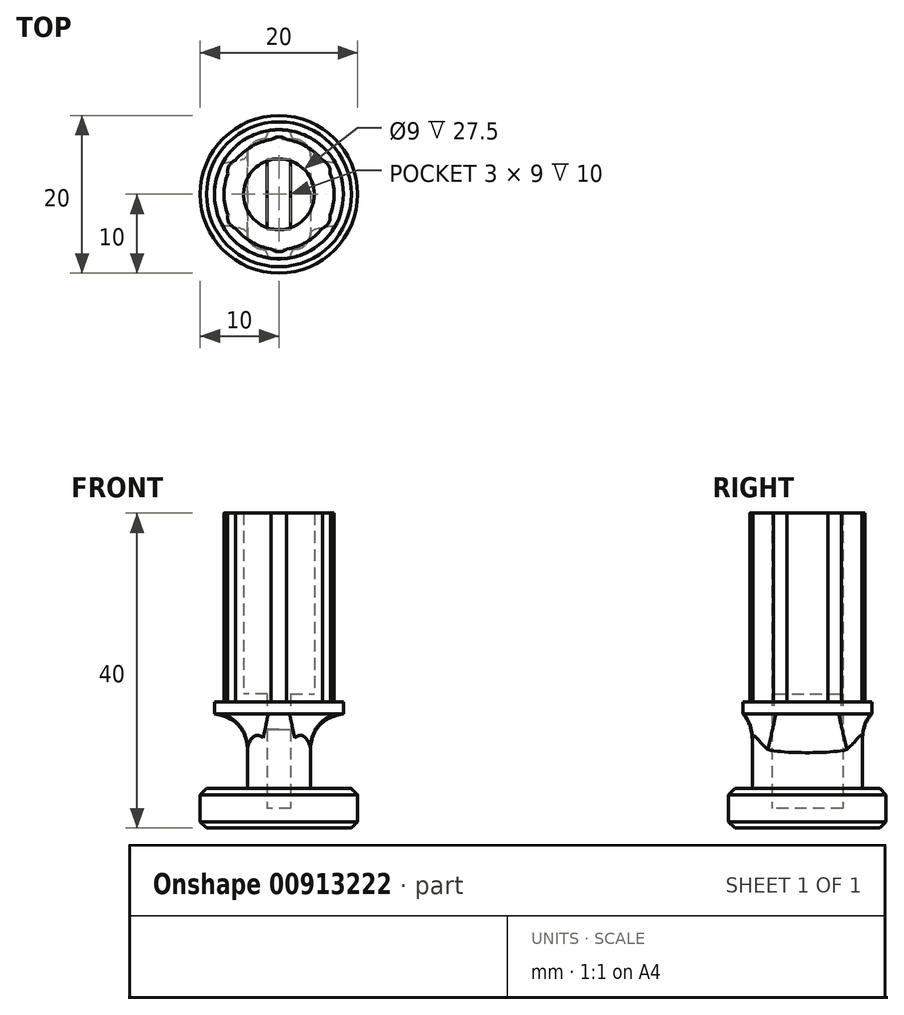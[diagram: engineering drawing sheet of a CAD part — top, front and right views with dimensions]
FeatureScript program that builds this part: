
annotation { "Feature Type Name" : "Feature", "Feature Type Description" : "" }
export const myFeature = defineFeature(function(context is Context, id is Id, definition is map)
    precondition{}
    {
        {
            var Q0;
            Q0=qCreatedBy(makeId("Top.planeOp"),FACE);
            var sketch = newSketch(context, id + "F0", { "sketchPlane" : qUnion([Q0])});
            skCircle(sketch, "E0", {"center": v(0, 0) * mm, "radius": 10 * mm});
            skArc(sketch, "E1", {"start": v(-0.99, 6.93) * mm, "mid": v(-3.5, 6.06) * mm, "end": v(-5.5, 4.32) * mm});
            skArc(sketch, "E2", {"start": v(0.99, 6.93) * mm, "mid": v(0, 7.3) * mm, "end": v(-0.99, 6.93) * mm});
            skArc(sketch, "E3.1.0", {"start": v(-5.5, 4.32) * mm, "mid": v(-6.32, 3.65) * mm, "end": v(-6.5, 2.61) * mm});
            skArc(sketch, "E3.2.0", {"start": v(-6.5, -2.61) * mm, "mid": v(-6.32, -3.65) * mm, "end": v(-5.5, -4.32) * mm});
            skArc(sketch, "E3.3.0", {"start": v(-0.99, -6.93) * mm, "mid": v(0, -7.3) * mm, "end": v(0.99, -6.93) * mm});
            skArc(sketch, "E3.4.0", {"start": v(5.5, -4.32) * mm, "mid": v(6.32, -3.65) * mm, "end": v(6.5, -2.61) * mm});
            skArc(sketch, "E3.5.0", {"start": v(6.5, 2.61) * mm, "mid": v(6.32, 3.65) * mm, "end": v(5.5, 4.32) * mm});
            skArc(sketch, "E4.trimOffspring", {"start": v(5.5, 4.32) * mm, "mid": v(3.5, 6.06) * mm, "end": v(0.99, 6.93) * mm});
            skArc(sketch, "E5.trimOffspring", {"start": v(-6.5, 2.61) * mm, "mid": v(-7, 0) * mm, "end": v(-6.5, -2.61) * mm});
            skArc(sketch, "E6.trimOffspring", {"start": v(-5.5, -4.32) * mm, "mid": v(-3.5, -6.06) * mm, "end": v(-0.99, -6.93) * mm});
            skArc(sketch, "E7.trimOffspring", {"start": v(0.99, -6.93) * mm, "mid": v(3.5, -6.06) * mm, "end": v(5.5, -4.32) * mm});
            skArc(sketch, "E8.trimOffspring", {"start": v(6.5, -2.61) * mm, "mid": v(7, 0) * mm, "end": v(6.5, 2.61) * mm});
            skPoint(sketch, "E9.middle", {"position": v(-0.44, -0.52) * mm});
            skCircle(sketch, "E10.0", {"center": v(0, 0) * mm, "radius": 8.2 * mm});
            skSolve(sketch);
        }
        {
            var Q0;
            Q0=makeQuery(id+"F0.imprint","IMPRINT",FACE,{"disambiguationData":[TD([[makeQuery(id+"F0.imprint","IMPRINT",EDGE,{"derivedFrom":sQuery(id+"F0.wireOp",EDGE,"E0")}),1.0]])]});
            var Q1;
            Q1=makeQuery(id+"F0.imprint","IMPRINT",FACE,{"disambiguationData":[TD([[makeQuery(id+"F0.imprint","IMPRINT",EDGE,{"derivedFrom":sQuery(id+"F0.wireOp",EDGE,"E1")}),-1.0]])]});
            extrude(context, id + "F1", {"entities" : qUnion([Q0, Q1]), "depth" : 5 * mm, "offsetDistance" : 25 * mm});
        }
        {
            var Q0;
            Q0=makeQuery(id+"F1.opExtrude","CAP_EDGE",EDGE,{"disambiguationData":[OSD([sQuery(id+"F0.wireOp",EDGE,"E0")])],"isStart":true});
            var Q1;
            Q1=makeQuery(id+"F1.opExtrude","CAP_EDGE",EDGE,{"disambiguationData":[OSD([sQuery(id+"F0.wireOp",EDGE,"E0")])],"isStart":false});
            chamfer(context, id + "F2", {"entities" : qUnion([Q0, Q1]), "width" : .8 * mm, "tangentPropagation" : true});
        }
        {
            var Q0;
            Q0=qCreatedBy(makeId("Top.planeOp"),FACE);
            var sketch = newSketch(context, id + "F3", { "sketchPlane" : qUnion([Q0])});
            skLineSegment(sketch, "E11.bottom", {"start": v(-4, -7) * mm, "end": v(4, -7) * mm});
            skLineSegment(sketch, "E11.top", {"start": v(-4, 7) * mm, "end": v(4, 7) * mm});
            skLineSegment(sketch, "E11.left", {"start": v(-4, -7) * mm, "end": v(-4, 7) * mm});
            skLineSegment(sketch, "E11.right", {"start": v(4, -7) * mm, "end": v(4, 7) * mm});
            skPoint(sketch, "E11.middle", {"position": v(0, 0) * mm});
            skSolve(sketch);
        }
        {
            var Q0;
            Q0 = qSketchRegion(id + "F3", true);
            extrude(context, id + "F4", {"entities" : qUnion([Q0]), "operationType" : NewBodyOperationType.ADD, "depth" : 15 * mm, "offsetDistance" : 25 * mm, "hasSecondDirection" : true, "secondDirectionOppositeDirection" : false, "secondDirectionDepth" : 2 * mm});
        }
        {
            var Q0;
            {var subQ1=sQuery(id+"F0.wireOp",EDGE,"E3.4.0");Q0=makeQuery(id+"F0.imprint","IMPRINT",FACE,{"disambiguationData":[TD([[makeQuery(id+"F0.imprint","IMPRINT",EDGE,{"derivedFrom":subQ1}),1.0]])]});}
            var Q1;
            {var subQ1=sQuery(id+"F0.wireOp",EDGE,"E3.1.0");Q1=makeQuery(id+"F0.imprint","IMPRINT",FACE,{"disambiguationData":[TD([[makeQuery(id+"F0.imprint","IMPRINT",EDGE,{"derivedFrom":subQ1}),1.0]])]});}
            var Q2;
            Q2=makeQuery(id+"F3.imprint","IMPRINT",FACE,{"disambiguationData":[TD([[makeQuery(id+"F3.imprint","IMPRINT",EDGE,{"derivedFrom":sQuery(id+"F3.wireOp",EDGE,"E11.bottom")}),1.0]])]});
            extrude(context, id + "F5", {"entities" : qUnion([Q0, Q1, Q2]), "operationType" : NewBodyOperationType.ADD, "depth" : 5 * mm, "offsetDistance" : 25 * mm});
        }
        {
            var Q0;
            {var subQ1=sQuery(id+"F0.wireOp",EDGE,"E3.4.0");Q0=makeQuery(id+"F0.imprint","IMPRINT",FACE,{"disambiguationData":[TD([[makeQuery(id+"F0.imprint","IMPRINT",EDGE,{"derivedFrom":subQ1}),1.0]])]});}
            var Q1;
            {var subQ1=sQuery(id+"F0.wireOp",EDGE,"E3.1.0");Q1=makeQuery(id+"F0.imprint","IMPRINT",FACE,{"disambiguationData":[TD([[makeQuery(id+"F0.imprint","IMPRINT",EDGE,{"derivedFrom":subQ1}),1.0]])]});}
            var Q2;
            {var subQ1=sQuery(id+"F0.wireOp",EDGE,"E2");Q2=makeQuery(id+"F0.imprint","IMPRINT",FACE,{"disambiguationData":[TD([[makeQuery(id+"F0.imprint","IMPRINT",EDGE,{"derivedFrom":subQ1}),1.0]])]});}
            extrude(context, id + "F6", {"entities" : qUnion([Q0, Q1, Q2]), "operationType" : NewBodyOperationType.ADD, "depth" : 40 * mm, "offsetDistance" : 25 * mm, "hasSecondDirection" : true, "secondDirectionOppositeDirection" : false, "secondDirectionDepth" : 14.5 * mm});
        }
        {
            var Q0;
            Q0=makeQuery(id+"F6.opExtrude","CAP_FACE",FACE,{"disambiguationData":[OSD([sQuery(id+"F0.wireOp",EDGE,"E1"),sQuery(id+"F0.wireOp",EDGE,"E2"),sQuery(id+"F0.wireOp",EDGE,"E3.1.0"),sQuery(id+"F0.wireOp",EDGE,"E3.2.0"),sQuery(id+"F0.wireOp",EDGE,"E3.3.0"),sQuery(id+"F0.wireOp",EDGE,"E3.4.0"),sQuery(id+"F0.wireOp",EDGE,"E3.5.0"),sQuery(id+"F0.wireOp",EDGE,"E4.trimOffspring"),sQuery(id+"F0.wireOp",EDGE,"E5.trimOffspring"),sQuery(id+"F0.wireOp",EDGE,"E6.trimOffspring"),sQuery(id+"F0.wireOp",EDGE,"E7.trimOffspring"),sQuery(id+"F0.wireOp",EDGE,"E8.trimOffspring")])],"isStart":false});
            shell(context, id + "F7", {"entities" : qUnion([Q0]), "thickness" : 2.5 * mm});
        }
        {
            var Q0;
            Q0=makeQuery(id+"F0.imprint","IMPRINT",FACE,{"disambiguationData":[TD([[makeQuery(id+"F0.imprint","IMPRINT",EDGE,{"derivedFrom":sQuery(id+"F0.wireOp",EDGE,"E1")}),-1.0]])]});
            extrude(context, id + "F8", {"entities" : qUnion([Q0]), "operationType" : NewBodyOperationType.ADD, "depth" : 16 * mm, "offsetDistance" : 25 * mm, "hasSecondDirection" : true, "secondDirectionOppositeDirection" : false, "secondDirectionDepth" : 14.5 * mm});
        }
        {
            var Q0;
            Q0=makeQuery(id+"F4.opExtrude","SWEPT_EDGE",EDGE,{"disambiguationData":[OSD([sQuery(id+"F3.wireOp",EDGE,"E11.bottom"),sQuery(id+"F3.wireOp",EDGE,"E11.right")])]});
            var Q1;
            Q1=makeQuery(id+"F4.opExtrude","SWEPT_EDGE",EDGE,{"disambiguationData":[OSD([sQuery(id+"F3.wireOp",EDGE,"E11.bottom"),sQuery(id+"F3.wireOp",EDGE,"E11.left")])]});
            var Q2;
            Q2=makeQuery(id+"F4.opExtrude","SWEPT_EDGE",EDGE,{"disambiguationData":[OSD([sQuery(id+"F3.wireOp",EDGE,"E11.top"),sQuery(id+"F3.wireOp",EDGE,"E11.right")])]});
            var Q3;
            Q3=makeQuery(id+"F4.opExtrude","SWEPT_EDGE",EDGE,{"disambiguationData":[OSD([sQuery(id+"F3.wireOp",EDGE,"E11.top"),sQuery(id+"F3.wireOp",EDGE,"E11.left")])]});
            fillet(context, id + "F9", {"entities" : qUnion([Q0, Q1, Q2, Q3]), "radius" : 2 * mm, "tangentPropagation" : true, "allowEdgeOverflow" : false});
        }
        {
            var Q0;
            Q0=makeQuery(id+"F8.boolean.opBoolean","INTERSECT",EDGE,{"derivedFrom":[makeQuery(id+"F4.opExtrude","SWEPT_FACE",FACE,{"disambiguationData":[OSD([sQuery(id+"F3.wireOp",EDGE,"E11.left")])]}),makeQuery(id+"F8.opExtrude","CAP_FACE",FACE,{"disambiguationData":[OSD([sQuery(id+"F0.wireOp",EDGE,"E1"),sQuery(id+"F0.wireOp",EDGE,"E2"),sQuery(id+"F0.wireOp",EDGE,"E3.1.0"),sQuery(id+"F0.wireOp",EDGE,"E3.2.0"),sQuery(id+"F0.wireOp",EDGE,"E3.3.0"),sQuery(id+"F0.wireOp",EDGE,"E3.4.0"),sQuery(id+"F0.wireOp",EDGE,"E3.5.0"),sQuery(id+"F0.wireOp",EDGE,"E4.trimOffspring"),sQuery(id+"F0.wireOp",EDGE,"E5.trimOffspring"),sQuery(id+"F0.wireOp",EDGE,"E6.trimOffspring"),sQuery(id+"F0.wireOp",EDGE,"E7.trimOffspring"),sQuery(id+"F0.wireOp",EDGE,"E8.trimOffspring"),sQuery(id+"F0.wireOp",EDGE,"E10.0")])],"isStart":true})]});
            fillet(context, id + "F10", {"entities" : qUnion([Q0]), "radius" : 5 * mm, "tangentPropagation" : true, "rho" : 0.5, "crossSection" : FilletCrossSection.CONIC, "allowEdgeOverflow" : false});
        }
    });
